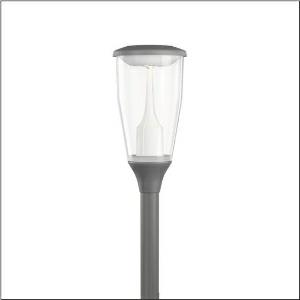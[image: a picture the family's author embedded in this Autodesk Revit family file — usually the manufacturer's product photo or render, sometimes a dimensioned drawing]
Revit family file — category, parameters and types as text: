
# Revit family: dl_11_iq___st1_2a_5xa5575ef14h000022_0b87
name_source: partatom
category: Lighting Fixtures
units: mm (PartAtom-declared; Revit-internal decimal feet)

## family parameters
Cut with Voids When Loaded = No
Host = Face
Light Source = No
Part Type = Normal
Room Calculation Point = No
Round Connector Dimension = Use Diameter
Shared = No

## types (1)
- --- (1 x LED, 1560 lm, 10.5 W, 3000K)
    Apparent Load = 11 VA
    CIE Flux Codes = 24 63 94 96 100
    Color Rendering = 70
    Color Temperature = 3000K
    Default Elevation = 1800 mm
    Description = DL 11 iQ, mast luminaire, Module 540 iQ-SR, primary light control with 3 zone facetted reflector, of plastic, silver coated, highly specular, structured, primary optical cover: cover, of PMMA, transparent, light distribution: ST1.2a, light emission: direct distribution, primary light characteristic: asymmetric, installation type: post-top, LED, High Power LED, rated luminous flux: 1.560lm, luminous efficacy: 149lm/W, light colour: 730, colour temperature: 3000K, control gear: iQ Street-Remote, control: Street-Remote, Auto-Match, Temp-Guard, Lumen-Switch, Night-Set, Smart-Wire, Light-Fading, Desk-Remote (wireless, voltage-free reading and setting of iQ features in the workshop via application-optimized NFC function/RFID function), optimised constant luminous flux control (CLO 2.0), mains connection: 220..240V, AC, 50/60Hz, connection cable pre-assembled, cable length: 5,5m, start of lifetime: 11W, end of service life: 11W, reduction: 5W, luminaire housing, upper part, of diecast aluminium, coated, Siteco® metallic grey (DB 702S), spigot size: 76mm (post-top), mounting height: 3..5m, post-top mast mounting element, of diecast aluminium, coated, Siteco® metallic grey (DB 702S), Module 540 iQ-SR, traffic white (RAL 9016), equipment: standard, protection rating (complete): IP66, insulation class (complete): insulation class II (safety insulation), certification: CE, ENEC, ENEC+, VDE, impact resistance: IK07, packaging unit: 1 piece

Light Distribution: ST1.2a
    Height = 665 mm
    Lamp = 1 x LED
    Lamp Light Flux = 1560 lm
    Lamp Power = 10.5 W
    Lamp count = 1
    Length = 334 mm
    Luminous efficacy = 149 lm/W
    Manufacturer = Siteco
    ModVariant = No
    Model = 5XA5575EF14H000022
    Number of Poles = 1
    OnlyDefault = Yes
    Power Factor = 1
    Product Name = DL 11 iQ | ST1.2a
    Product group = mast luminaire | pylon top
    ProductGroupID = 6100
    Protection Class = Protection class II
    Protection Degree = IP 66
    RLX_Detail_Level = 1
    RLX_Emergency_Light_Flux = 0 lm
    RLX_Emergency_Type = 0
    RLX_Emergency_Type_DB = No
    RlxData = <blob elided: 139429 chars, md5=6ac095c7>
    Socket = socket
    Standby Power = 0 W
    System Light Flux = 1560 lm
    System Power = 11 W
    Type Comments = factory setting: luminous flux: 100 % | dim-lin: 254 | 419 mA
    Type Image = l_1258354.jpg
    URL = http://relux.com
    VarID = @adj_116489
    Voltage = 0 V
    Weight = 0.00 kg
    Width = 0 mm  [stored 0 ft]

note: [stored X ft] marks values corroborated as IEEE doubles in the binary element streams (Revit-internal decimal feet)

## geometry (parser evidence)
native form markers: Blend x4, Sweep x11
no freeform markers — native parametric forms only
